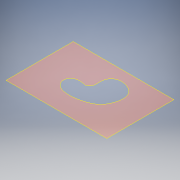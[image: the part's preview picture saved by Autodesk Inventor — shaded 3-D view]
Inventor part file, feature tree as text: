
AUTODESK INVENTOR PART (.ipt)
format: ipt  version: 2018 (Build 220112000, 112)  size: 97,792 bytes
history: native  units: mm
features: sketch x1, other x1, surface_op x1
ambient origin geometry x8: Origin, YZ Plane, XZ Plane, XY Plane, X Axis, Y Axis, Z Axis, Center Point
bodies: Body1 (feature_tree)
feature tree (3):
  sketch  "Sketch1"  dims[d0=150.0mm d1=100.0mm]
  other  "Srf1"
  surface_op  "Boundary Patch1"
